# Revit family: Trash Receptacle Collection
name_source: partatom
category: Furniture
units: mm (PartAtom-declared; Revit-internal decimal feet)

## family parameters
Always vertical = Yes
Cut with Voids When Loaded = No
OmniClass Number = 23.40.20.00
OmniClass Title = General Furniture and Specialties
Room Calculation Point = No
Shared = No
Work Plane-Based = No

## types (8) — shared parameters
Default Elevation = 0' - 0"
Trash Body Material = RAL7001 GREY
Trash Top Material = RAL7001 GREY

## per-type parameters (varying)
| type | 12"x16" - Recycling Opening | 12"x16" - Trash Can | 12"x16" - Waste Opening | 14"x18" - Recycling Opening | 14"x18" - Trash Can | 14"x18" - Waste Opening | 16"x16" - Recycling Opening | 16"x16" - Trash Can | 16"x16" - Waste Opening | 18"x18" - Recycling Opening | 18"x18" - Trash Can | 18"x18" - Waste Opening |
| 28 1/4" Tall - Narrow 12"x 16" - Recycle | Yes | Yes | No | No | No | No | No | No | No | No | No | No |
| 28 1/4" Tall - Wide 16"x 16" - Recycle | No | No | No | No | No | No | Yes | Yes | No | No | No | No |
| 33 1/4" Tall - Narrow 14"x 18" - Waste | No | No | No | No | Yes | Yes | No | No | No | No | No | No |
| 33 1/4" Tall - Wide 18"x 18" - Waste | No | No | No | No | No | No | No | No | No | No | Yes | Yes |
| 28 1/4" Tall - Narrow 12"x 16" - Waste | No | Yes | Yes | No | No | No | No | No | No | No | No | No |
| 28 1/4" Tall - Wide 16"x 16" - Waste | No | No | No | No | No | No | No | Yes | Yes | No | No | No |
| 33 1/4" Tall - Narrow 14"x 18" - Recycle | No | No | No | Yes | Yes | No | No | No | No | No | No | No |
| 33 1/4" Tall - Wide 18"x 18" - Recycle | No | No | No | No | No | No | No | No | No | Yes | Yes | No |

## geometry (parser evidence)
native form markers: Sweep x2
no freeform markers — native parametric forms only
